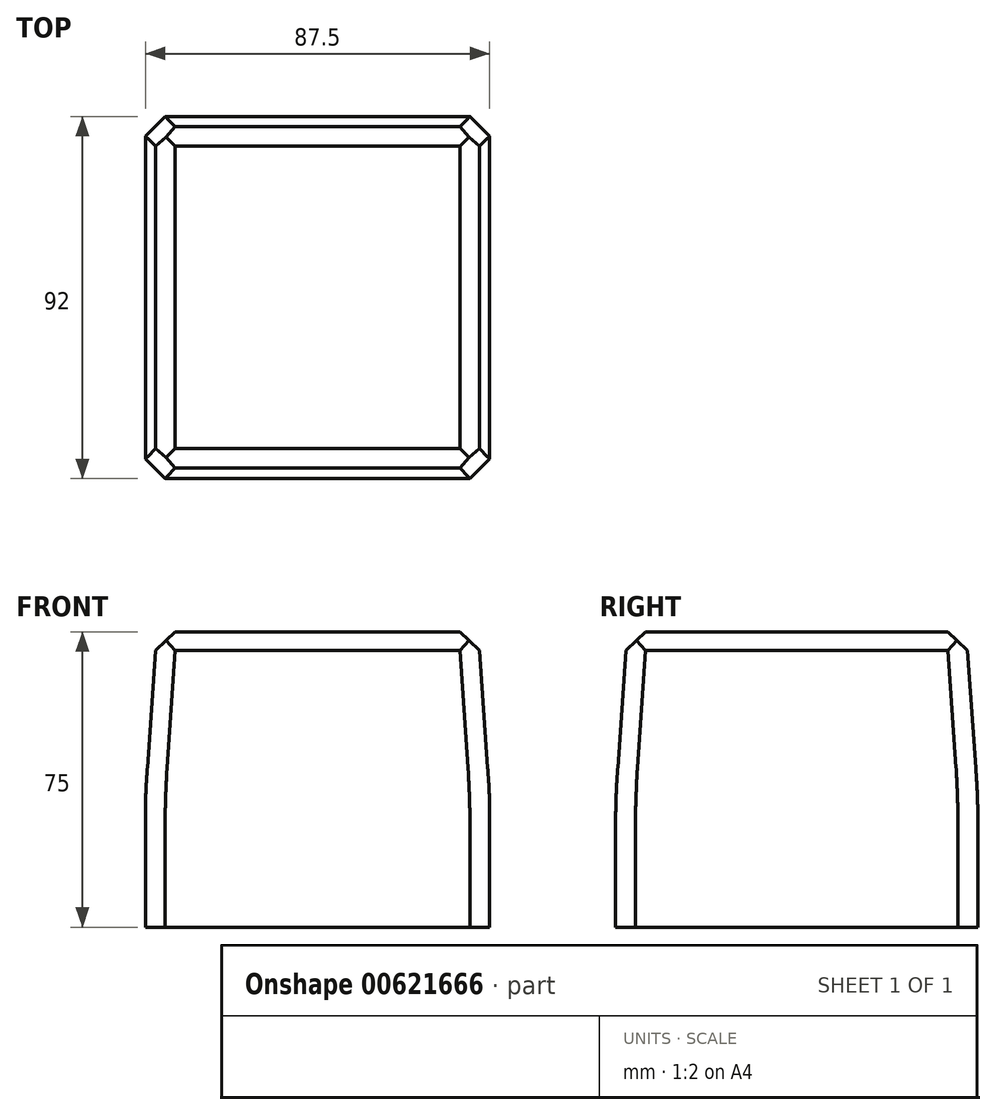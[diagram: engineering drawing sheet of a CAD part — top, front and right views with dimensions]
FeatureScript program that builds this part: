
annotation { "Feature Type Name" : "Feature", "Feature Type Description" : "" }
export const myFeature = defineFeature(function(context is Context, id is Id, definition is map)
    precondition{}
    {
        {
            var Q0;
            Q0=qCreatedBy(makeId("Top.planeOp"),FACE);
            var sketch = newSketch(context, id + "F0", { "sketchPlane" : qUnion([Q0])});
            skLineSegment(sketch, "E0.bottom", {"start": v(43.75, -47.41) * mm, "end": v(-43.75, -47.41) * mm});
            skLineSegment(sketch, "E0.top", {"start": v(43.75, 44.59) * mm, "end": v(-43.75, 44.59) * mm});
            skLineSegment(sketch, "E0.left", {"start": v(43.75, -47.41) * mm, "end": v(43.75, 44.59) * mm});
            skLineSegment(sketch, "E0.right", {"start": v(-43.75, -47.41) * mm, "end": v(-43.75, 44.59) * mm});
            skPoint(sketch, "E0.middle", {"position": v(0, -1.41) * mm});
            skSolve(sketch);
        }
        {
            var Q0;
            Q0 = qSketchRegion(id + "F0", true);
            extrude(context, id + "F1", {"entities" : qUnion([Q0]), "depth" : 42 * mm, "offsetDistance" : 25 * mm, "hasDraft" : true, "draftAngle" : 4 * degree, "draftPullDirection" : true, "hasSecondDirection" : true, "secondDirectionOppositeDirection" : true, "secondDirectionDepth" : 33 * mm});
        }
        {
            var Q0;
            Q0=makeQuery(id+"F1.opExtrude","CAP_FACE",FACE,{"disambiguationData":[OSD([sQuery(id+"F0.wireOp",EDGE,"E0.bottom"),sQuery(id+"F0.wireOp",EDGE,"E0.top"),sQuery(id+"F0.wireOp",EDGE,"E0.left"),sQuery(id+"F0.wireOp",EDGE,"E0.right")])],"isStart":false});
            var sketch = newSketch(context, id + "F2", { "sketchPlane" : qUnion([Q0])});
            skLineSegment(sketch, "E1", {"start": v(14.62, 37.08) * mm, "end": v(-35.6, 36.55) * mm});
            skLineSegment(sketch, "E2", {"start": v(-35.6, 36.55) * mm, "end": v(-36.91, -10.79) * mm});
            skLineSegment(sketch, "E3", {"start": v(-36.91, -10.79) * mm, "end": v(14.62, 37.08) * mm});
            skSolve(sketch);
        }
        {
            var Q0;
            Q0=makeQuery(id+"F2.imprint","IMPRINT",FACE,{"disambiguationData":[TD([[makeQuery(id+"F2.imprint","IMPRINT",EDGE,{"derivedFrom":sQuery(id+"F2.wireOp",EDGE,"E1")}),-1.0]])]});
            cPlane(context, id + "F3", {"entities" : qUnion([Q0]), "cplaneType" : CPlaneType.OFFSET, "offset" : 24 * mm, "oppositeDirection" : true, "width" : 150 * mm, "height" : 150 * mm});
        }
        {
            var Q0;
            Q0=makeQuery(id+"F1.opExtrude","CAP_FACE",FACE,{"disambiguationData":[OSD([sQuery(id+"F0.wireOp",EDGE,"E0.bottom"),sQuery(id+"F0.wireOp",EDGE,"E0.top"),sQuery(id+"F0.wireOp",EDGE,"E0.left"),sQuery(id+"F0.wireOp",EDGE,"E0.right")])],"isStart":false});
            cPlane(context, id + "F4", {"entities" : qUnion([Q0]), "cplaneType" : CPlaneType.OFFSET, "offset" : 21 * mm, "oppositeDirection" : true, "width" : 150 * mm, "height" : 150 * mm});
        }
        {
            var Q0;
            Q0=makeQuery(id+"F1.opExtrude","CAP_FACE",FACE,{"disambiguationData":[OSD([sQuery(id+"F0.wireOp",EDGE,"E0.bottom"),sQuery(id+"F0.wireOp",EDGE,"E0.top"),sQuery(id+"F0.wireOp",EDGE,"E0.left"),sQuery(id+"F0.wireOp",EDGE,"E0.right")])],"isStart":false});
            chamfer(context, id + "F5", {"entities" : qUnion([Q0]), "width" : 5 * mm, "tangentPropagation" : true});
        }
        {
            var Q0;
            Q0=makeQuery(id+"F1.opExtrude","SWEPT_EDGE",EDGE,{"disambiguationData":[OSD([sQuery(id+"F0.wireOp",EDGE,"E0.top"),sQuery(id+"F0.wireOp",EDGE,"E0.left")])]});
            var Q1;
            Q1=makeQuery(id+"F1.opExtrude","SWEPT_EDGE",EDGE,{"disambiguationData":[OSD([sQuery(id+"F0.wireOp",EDGE,"E0.top"),sQuery(id+"F0.wireOp",EDGE,"E0.right")])]});
            var Q2;
            Q2=makeQuery(id+"F1.opExtrude","SWEPT_EDGE",EDGE,{"disambiguationData":[OSD([sQuery(id+"F0.wireOp",EDGE,"E0.bottom"),sQuery(id+"F0.wireOp",EDGE,"E0.right")])]});
            var Q3;
            Q3=makeQuery(id+"F1.opExtrude","SWEPT_EDGE",EDGE,{"disambiguationData":[OSD([sQuery(id+"F0.wireOp",EDGE,"E0.bottom"),sQuery(id+"F0.wireOp",EDGE,"E0.left")])]});
            chamfer(context, id + "F6", {"entities" : qUnion([Q0, Q1, Q2, Q3]), "width" : 5 * mm, "tangentPropagation" : true});
        }
        {
            var Q0;
            {var subQ0=makeQuery(id+"F1.opExtrude","SWEPT_FACE",FACE,{"disambiguationData":[OSD([sQuery(id+"F0.wireOp",EDGE,"E0.bottom")])]});Q0=makeQuery(id+"F1.*.booleanUnion.opBoolean","MERGE",EDGE,{"derivedFrom":[makeQuery(id+"F1.*.split.splitOp","SPLIT_SURFACE_INTERSECT",EDGE,{"derivedFrom":[subQ0]}),makeQuery(id+"F1.*.split.splitOp","SPLIT_SURFACE_INTERSECT",EDGE,{"derivedFrom":[subQ0],"isFromBackBody":true})]});}
            var Q1;
            {var subQ0=makeQuery(id+"F1.opExtrude","SWEPT_EDGE",EDGE,{"disambiguationData":[OSD([sQuery(id+"F0.wireOp",EDGE,"E0.bottom"),sQuery(id+"F0.wireOp",EDGE,"E0.left")])]});Q1=makeQuery(id+"F6.opChamfer","BLEND_EDGE",EDGE,{"blendedFrom":[makeQuery(id+"F1.*.split.splitOp","SPLIT",EDGE,{"derivedFrom":subQ0,"isFromBackBody":true}),makeQuery(id+"F1.*.split.splitOp","SPLIT",EDGE,{"derivedFrom":subQ0})],"blendedInto":[]});}
            var Q2;
            {var subQ0=makeQuery(id+"F1.opExtrude","SWEPT_FACE",FACE,{"disambiguationData":[OSD([sQuery(id+"F0.wireOp",EDGE,"E0.left")])]});Q2=makeQuery(id+"F1.*.booleanUnion.opBoolean","MERGE",EDGE,{"derivedFrom":[makeQuery(id+"F1.*.split.splitOp","SPLIT_SURFACE_INTERSECT",EDGE,{"derivedFrom":[subQ0]}),makeQuery(id+"F1.*.split.splitOp","SPLIT_SURFACE_INTERSECT",EDGE,{"derivedFrom":[subQ0],"isFromBackBody":true})]});}
            var Q3;
            {var subQ0=makeQuery(id+"F1.opExtrude","SWEPT_EDGE",EDGE,{"disambiguationData":[OSD([sQuery(id+"F0.wireOp",EDGE,"E0.bottom"),sQuery(id+"F0.wireOp",EDGE,"E0.right")])]});Q3=makeQuery(id+"F6.opChamfer","BLEND_EDGE",EDGE,{"blendedFrom":[makeQuery(id+"F1.*.split.splitOp","SPLIT",EDGE,{"derivedFrom":subQ0,"isFromBackBody":true}),makeQuery(id+"F1.*.split.splitOp","SPLIT",EDGE,{"derivedFrom":subQ0})],"blendedInto":[]});}
            var Q4;
            {var subQ0=makeQuery(id+"F1.opExtrude","SWEPT_FACE",FACE,{"disambiguationData":[OSD([sQuery(id+"F0.wireOp",EDGE,"E0.right")])]});Q4=makeQuery(id+"F1.*.booleanUnion.opBoolean","MERGE",EDGE,{"derivedFrom":[makeQuery(id+"F1.*.split.splitOp","SPLIT_SURFACE_INTERSECT",EDGE,{"derivedFrom":[subQ0]}),makeQuery(id+"F1.*.split.splitOp","SPLIT_SURFACE_INTERSECT",EDGE,{"derivedFrom":[subQ0],"isFromBackBody":true})]});}
            var Q5;
            {var subQ0=makeQuery(id+"F1.opExtrude","SWEPT_EDGE",EDGE,{"disambiguationData":[OSD([sQuery(id+"F0.wireOp",EDGE,"E0.top"),sQuery(id+"F0.wireOp",EDGE,"E0.right")])]});Q5=makeQuery(id+"F6.opChamfer","BLEND_EDGE",EDGE,{"blendedFrom":[makeQuery(id+"F1.*.split.splitOp","SPLIT",EDGE,{"derivedFrom":subQ0,"isFromBackBody":true}),makeQuery(id+"F1.*.split.splitOp","SPLIT",EDGE,{"derivedFrom":subQ0})],"blendedInto":[]});}
            var Q6;
            {var subQ0=makeQuery(id+"F1.opExtrude","SWEPT_FACE",FACE,{"disambiguationData":[OSD([sQuery(id+"F0.wireOp",EDGE,"E0.top")])]});Q6=makeQuery(id+"F1.*.booleanUnion.opBoolean","MERGE",EDGE,{"derivedFrom":[makeQuery(id+"F1.*.split.splitOp","SPLIT_SURFACE_INTERSECT",EDGE,{"derivedFrom":[subQ0]}),makeQuery(id+"F1.*.split.splitOp","SPLIT_SURFACE_INTERSECT",EDGE,{"derivedFrom":[subQ0],"isFromBackBody":true})]});}
            var Q7;
            {var subQ0=makeQuery(id+"F1.opExtrude","SWEPT_EDGE",EDGE,{"disambiguationData":[OSD([sQuery(id+"F0.wireOp",EDGE,"E0.top"),sQuery(id+"F0.wireOp",EDGE,"E0.left")])]});Q7=makeQuery(id+"F6.opChamfer","BLEND_EDGE",EDGE,{"blendedFrom":[makeQuery(id+"F1.*.split.splitOp","SPLIT",EDGE,{"derivedFrom":subQ0,"isFromBackBody":true}),makeQuery(id+"F1.*.split.splitOp","SPLIT",EDGE,{"derivedFrom":subQ0})],"blendedInto":[]});}
            fillet(context, id + "F7", {"entities" : qUnion([Q0, Q1, Q2, Q3, Q4, Q5, Q6, Q7]), "radius" : 150 * mm, "tangentPropagation" : true, "allowEdgeOverflow" : false});
        }
    });
